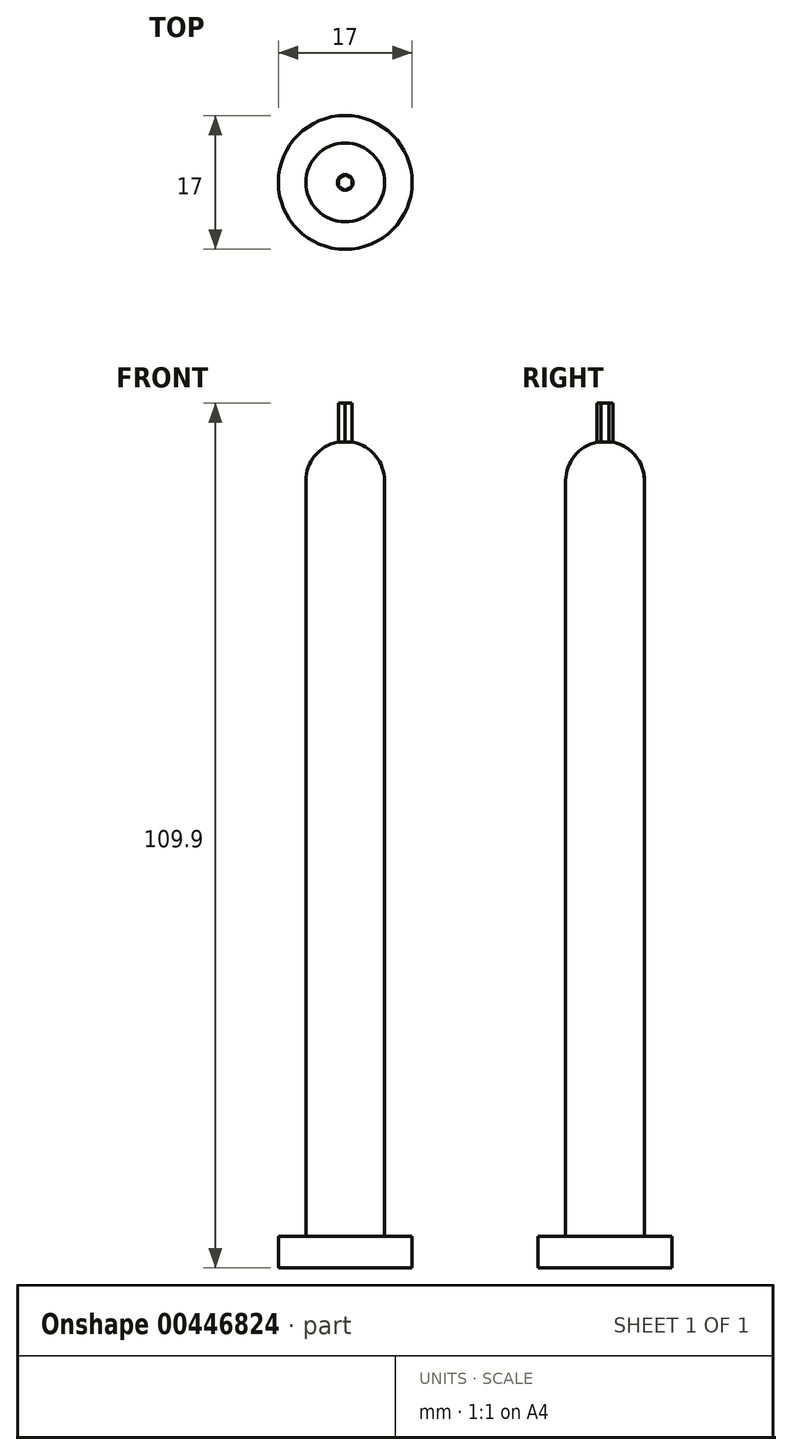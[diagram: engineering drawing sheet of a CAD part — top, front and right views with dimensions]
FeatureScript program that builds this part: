
annotation { "Feature Type Name" : "Feature", "Feature Type Description" : "" }
export const myFeature = defineFeature(function(context is Context, id is Id, definition is map)
    precondition{}
    {
        {
            var Q0;
            Q0=qCreatedBy(makeId("Top.planeOp"),FACE);
            var sketch = newSketch(context, id + "F0", { "sketchPlane" : qUnion([Q0])});
            skCircle(sketch, "E0", {"center": v(0, 0) * mm, "radius": 8.5 * mm});
            skSolve(sketch);
        }
        {
            var Q0;
            Q0=qSketchRegion(id+"F0",true);
            extrude(context, id + "F1", {"entities" : qUnion([Q0]), "depth" : 4 * mm});
        }
        {
            var Q0;
            Q0=qCreatedBy(makeId("Top.planeOp"),FACE);
            var sketch = newSketch(context, id + "F2", { "sketchPlane" : qUnion([Q0])});
            skCircle(sketch, "E1", {"center": v(0, 0) * mm, "radius": 5 * mm});
            skSolve(sketch);
        }
        {
            var Q0;
            Q0=qSketchRegion(id+"F2",true);
            extrude(context, id + "F3", {"entities" : qUnion([Q0]), "operationType" : NewBodyOperationType.ADD, "depth" : 100 * mm});
        }
        {
            var Q0;
            Q0=qCreatedBy(makeId("Right.planeOp"),FACE);
            var sketch = newSketch(context, id + "F4", { "sketchPlane" : qUnion([Q0])});
            skLineSegment(sketch, "E2", {"start": v(0, 100) * mm, "end": v(5, 100) * mm});
            skArc(sketch, "E3", {"start": v(5, 100) * mm, "mid": v(3.54, 103.54) * mm, "end": v(0, 105) * mm});
            skLineSegment(sketch, "E4", {"start": v(1, 104.9) * mm, "end": v(0, 104.9) * mm});
            skLineSegment(sketch, "E5", {"start": v(0, 107.19) * mm, "end": v(0, 100) * mm});
            skLineSegment(sketch, "E6", {"start": v(-1.55, -2.92) * mm, "end": v(3.45, -2.92) * mm});
            skArc(sketch, "E7", {"start": v(3.45, -2.92) * mm, "mid": v(1.99, 0.62) * mm, "end": v(-1.55, 2.08) * mm});
            skLineSegment(sketch, "E8", {"start": v(-0.55, 1.98) * mm, "end": v(-1.55, 1.98) * mm});
            skLineSegment(sketch, "E9", {"start": v(-1.55, 4.27) * mm, "end": v(-1.55, -2.92) * mm});
            skLineSegment(sketch, "E10", {"start": v(-0.77, 48.54) * mm, "end": v(4.23, 48.54) * mm});
            skArc(sketch, "E11", {"start": v(4.23, 48.54) * mm, "mid": v(2.76, 52.08) * mm, "end": v(-0.77, 53.54) * mm});
            skLineSegment(sketch, "E12", {"start": v(0.23, 53.44) * mm, "end": v(-0.77, 53.44) * mm});
            skLineSegment(sketch, "E13", {"start": v(-0.77, 55.73) * mm, "end": v(-0.77, 48.54) * mm});
            skLineSegment(sketch, "E14", {"start": v(-2.32, -54.38) * mm, "end": v(2.68, -54.38) * mm});
            skArc(sketch, "E15", {"start": v(2.68, -54.38) * mm, "mid": v(1.22, -50.84) * mm, "end": v(-2.32, -49.38) * mm});
            skLineSegment(sketch, "E16", {"start": v(-1.32, -49.48) * mm, "end": v(-2.32, -49.48) * mm});
            skLineSegment(sketch, "E17", {"start": v(-2.32, -47.2) * mm, "end": v(-2.32, -54.38) * mm});
            skSolve(sketch);
        }
        {
            var Q0;
            Q0=sQuery(id+"F4.wireOp",EDGE,"E4");
            cPlane(context, id + "F5", {"entities" : qUnion([Q0]), "cplaneType" : CPlaneType.LINE_ANGLE, "offset" : 25 * mm, "angle" : 0 * degree, "width" : 150 * mm, "height" : 150 * mm});
        }
        {
            var Q0;
            Q0=qCreatedBy(makeId("Right.planeOp"),FACE);
            var sketch = newSketch(context, id + "F6", { "sketchPlane" : qUnion([Q0])});
            skLineSegment(sketch, "E18", {"start": v(0, 86.28) * mm, "end": v(0, 91.28) * mm});
            skLineSegment(sketch, "E19", {"start": v(0, 91.28) * mm, "end": v(4.32, 86.28) * mm});
            skLineSegment(sketch, "E20", {"start": v(4.32, 86.28) * mm, "end": v(0, 86.28) * mm});
            skLineSegment(sketch, "E21", {"start": v(0, 105) * mm, "end": v(0, 100) * mm});
            skLineSegment(sketch, "E22", {"start": v(0, 100) * mm, "end": v(5, 100) * mm});
            skArc(sketch, "E23", {"start": v(5, 100) * mm, "mid": v(3.54, 103.54) * mm, "end": v(0, 105) * mm});
            skSolve(sketch);
        }
        {
            var Q0;
            {var subQ0=sQuery(id+"F4.wireOp",EDGE,"E2");Q0=makeQuery(id+"F4.imprint","IMPRINT",FACE,{"disambiguationData":[TD([[makeQuery(id+"F4.imprint","IMPRINT",EDGE,{"derivedFrom":subQ0}),1.0]])]});}
            var Q1;
            Q1=sQuery(id+"F6.wireOp",EDGE,"E21");
            revolve(context, id + "F7", {"operationType" : NewBodyOperationType.ADD, "entities" : qUnion([Q0]), "axis" : qUnion([Q1]), "revolveType" : RevolveType.FULL});
        }
        {
            var Q0;
            Q0=qCreatedBy(id+"F5.planeOp",FACE);
            var sketch = newSketch(context, id + "F8", { "sketchPlane" : qUnion([Q0])});
            skCircle(sketch, "E24.cCircle", {"center": v(0, 0) * mm, "radius": 0.87 * mm, "construction": true});
            skLineSegment(sketch, "E24.0", {"start": v(0.87, 0.5) * mm, "end": v(0.87, -0.5) * mm});
            skLineSegment(sketch, "E24.1", {"start": v(0.87, -0.5) * mm, "end": v(0, -1) * mm});
            skLineSegment(sketch, "E24.2", {"start": v(0, -1) * mm, "end": v(-0.87, -0.5) * mm});
            skLineSegment(sketch, "E24.3", {"start": v(-0.87, -0.5) * mm, "end": v(-0.87, 0.5) * mm});
            skLineSegment(sketch, "E24.4", {"start": v(-0.87, 0.5) * mm, "end": v(0, 1) * mm});
            skLineSegment(sketch, "E24.5", {"start": v(0, 1) * mm, "end": v(0.87, 0.5) * mm});
            skPoint(sketch, "E24.0.midPoint", {"position": v(0.87, 0) * mm});
            skSolve(sketch);
        }
        {
            var Q0;
            Q0=makeQuery(id+"F8.imprint","IMPRINT",FACE,{"disambiguationData":[TD([[makeQuery(id+"F8.imprint","IMPRINT",EDGE,{"derivedFrom":sQuery(id+"F8.wireOp",EDGE,"E24.0")}),-1.0]])]});
            extrude(context, id + "F9", {"entities" : qUnion([Q0]), "operationType" : NewBodyOperationType.ADD, "oppositeDirection" : true, "depth" : 5 * mm});
        }
    });
